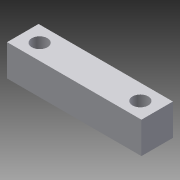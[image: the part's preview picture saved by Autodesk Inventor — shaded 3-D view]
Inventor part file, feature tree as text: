
AUTODESK INVENTOR PART (.ipt)
format: ipt  version: 2013 (Build 170138000, 138)  size: 82,432 bytes
history: native  units: mm
features: extrude x1, sketch x1
ambient origin geometry x8: Origin, YZ Plane, XZ Plane, XY Plane, X Axis, Y Axis, Z Axis, Center Point
bodies: Solid1 (feature_tree)
feature tree (2):
  extrude  "Extrusion1"  [1 undecoded]
  sketch  "Sketch1"  dims[d0=6.0mm d1=0.0mm]
note: 1 required parameter value undecoded (feature->parameter linkage not recoverable at this tier; creation-order binding heuristic only, values carry confidence <= 0.55)
